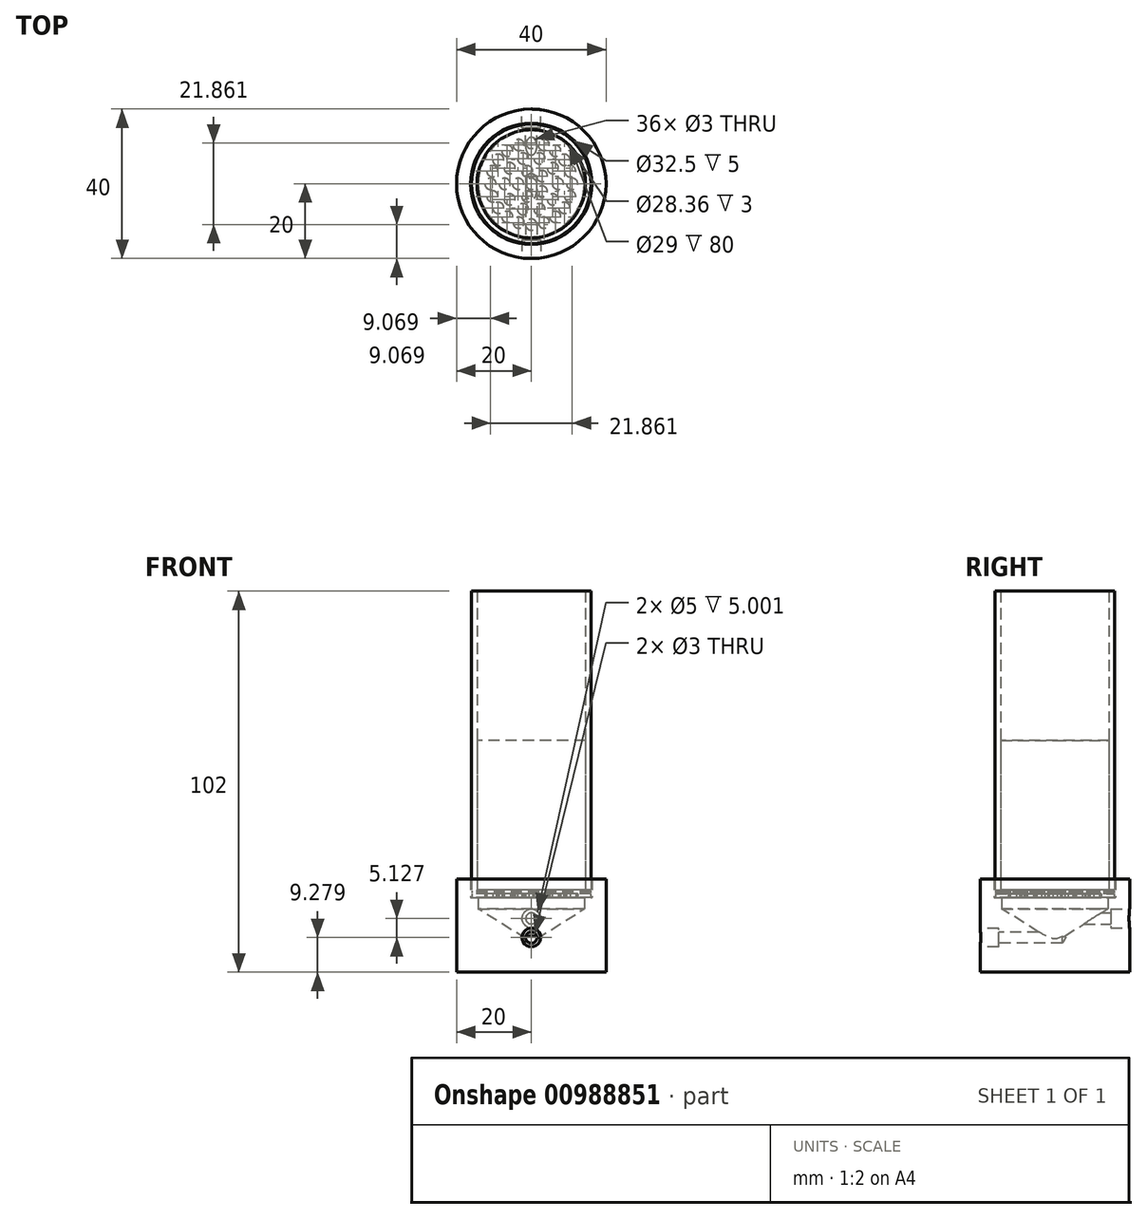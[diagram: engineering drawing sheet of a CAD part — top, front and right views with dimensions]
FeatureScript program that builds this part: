
annotation { "Feature Type Name" : "Feature", "Feature Type Description" : "" }
export const myFeature = defineFeature(function(context is Context, id is Id, definition is map)
    precondition{}
    {
        {
            var Q0;
            Q0=qCreatedBy(makeId("Top.planeOp"),FACE);
            var sketch = newSketch(context, id + "F0", { "sketchPlane" : qUnion([Q0])});
            skCircle(sketch, "E0", {"center": v(0, 0) * mm, "radius": 16 * mm});
            skCircle(sketch, "E1", {"center": v(0, 0) * mm, "radius": 14.5 * mm});
            skSolve(sketch);
        }
        {
            var Q0;
            Q0=makeQuery(id+"F0.imprint","IMPRINT",FACE,{"disambiguationData":[TD([[makeQuery(id+"F0.imprint","IMPRINT",EDGE,{"derivedFrom":sQuery(id+"F0.wireOp",EDGE,"E0")}),1.0]])]});
            extrude(context, id + "F1", {"entities" : qUnion([Q0]), "depth" : 80 * mm, "offsetDistance" : 25 * mm});
        }
        {
            var Q0;
            Q0=qCreatedBy(makeId("Front.planeOp"),FACE);
            var sketch = newSketch(context, id + "F2", { "sketchPlane" : qUnion([Q0])});
            skLineSegment(sketch, "E2", {"start": v(-16.25, 0) * mm, "end": v(-16.25, 5) * mm});
            skLineSegment(sketch, "E3", {"start": v(-16.25, 5) * mm, "end": v(-20, 5) * mm});
            skLineSegment(sketch, "E4", {"start": v(-20, 5) * mm, "end": v(-20, -20) * mm});
            skLineSegment(sketch, "E5", {"start": v(-20, -20) * mm, "end": v(0, -20) * mm});
            skLineSegment(sketch, "E6", {"start": v(0, -20) * mm, "end": v(0, -12) * mm});
            skLineSegment(sketch, "E7", {"start": v(0, -12) * mm, "end": v(-14.18, -3) * mm});
            skLineSegment(sketch, "E8", {"start": v(-14.18, -3) * mm, "end": v(-14.18, 0) * mm});
            skLineSegment(sketch, "E9", {"start": v(-14.18, 0) * mm, "end": v(-16.25, 0) * mm});
            skSolve(sketch);
        }
        {
            var Q0;
            Q0=makeQuery(id+"F2.imprint","IMPRINT",FACE,{"disambiguationData":[TD([[makeQuery(id+"F2.imprint","IMPRINT",EDGE,{"derivedFrom":sQuery(id+"F2.wireOp",EDGE,"E2")}),1.0]])]});
            var Q1;
            Q1=sQuery(id+"F2.wireOp",EDGE,"E6");
            revolve(context, id + "F3", {"surfaceOperationType" : NewSurfaceOperationType.NEW, "entities" : qUnion([Q0]), "axis" : qUnion([Q1]), "revolveType" : RevolveType.FULL});
        }
        {
            var Q0;
            Q0=qCreatedBy(makeId("Front.planeOp"),FACE);
            cPlane(context, id + "F4", {"entities" : qUnion([Q0]), "cplaneType" : CPlaneType.OFFSET, "offset" : 20 * mm, "width" : 150 * mm, "height" : 150 * mm});
        }
        {
            var Q0;
            Q0=qCreatedBy(id+"F4.planeOp",FACE);
            var sketch = newSketch(context, id + "F5", { "sketchPlane" : qUnion([Q0])});
            skLineSegment(sketch, "E10", {"start": v(0, -20.72) * mm, "end": v(0, -10.72) * mm});
            skSolve(sketch);
        }
        {
            var Q0;
            Q0=sQuery(id+"F5.wireOp",VERTEX,"E10.end");
            var Q1;
            Q1=makeQuery(id+"F3.opRevolve","SWEPT_BODY",BODY,{"disambiguationData":[OSD([sQuery(id+"F2.wireOp",EDGE,"E2"),sQuery(id+"F2.wireOp",EDGE,"E3"),sQuery(id+"F2.wireOp",EDGE,"E4"),sQuery(id+"F2.wireOp",EDGE,"E5"),sQuery(id+"F2.wireOp",EDGE,"E6"),sQuery(id+"F2.wireOp",EDGE,"E7"),sQuery(id+"F2.wireOp",EDGE,"E8"),sQuery(id+"F2.wireOp",EDGE,"E9")])]});
            hole(context, id + "F6", {"style" : HoleStyle.C_BORE, "endStyle" : HoleEndStyle.BLIND, "holeDiameter" : 3 * mm, "cBoreDiameter" : 5 * mm, "cBoreDepth" : 5 * mm, "majorDiameter" : 5 * mm, "holeDepth" : 22 * mm, "isTappedThrough" : true, "tappedDepth" : 12 * mm, "tapClearance" : 3, "startFromSketch" : true, "locations" : qUnion([Q0]), "scope" : qUnion([Q1])});
        }
        {
            var Q0;
            Q0=qCreatedBy(makeId("Front.planeOp"),FACE);
            cPlane(context, id + "F7", {"entities" : qUnion([Q0]), "cplaneType" : CPlaneType.OFFSET, "offset" : 20 * mm, "oppositeDirection" : true, "width" : 150 * mm, "height" : 150 * mm});
        }
        {
            var Q0;
            Q0=qCreatedBy(id+"F7.planeOp",FACE);
            var sketch = newSketch(context, id + "F8", { "sketchPlane" : qUnion([Q0])});
            skLineSegment(sketch, "E11", {"start": v(0, -19.77) * mm, "end": v(0, -5.6) * mm});
            skSolve(sketch);
        }
        {
            var Q0;
            Q0=sQuery(id+"F8.wireOp",VERTEX,"E11.end");
            var Q1;
            Q1=makeQuery(id+"F3.opRevolve","SWEPT_BODY",BODY,{"disambiguationData":[OSD([sQuery(id+"F2.wireOp",EDGE,"E2"),sQuery(id+"F2.wireOp",EDGE,"E3"),sQuery(id+"F2.wireOp",EDGE,"E4"),sQuery(id+"F2.wireOp",EDGE,"E5"),sQuery(id+"F2.wireOp",EDGE,"E6"),sQuery(id+"F2.wireOp",EDGE,"E7"),sQuery(id+"F2.wireOp",EDGE,"E8"),sQuery(id+"F2.wireOp",EDGE,"E9")])]});
            hole(context, id + "F9", {"style" : HoleStyle.C_BORE, "endStyle" : HoleEndStyle.BLIND, "oppositeDirection" : true, "holeDiameter" : 3 * mm, "cBoreDiameter" : 5 * mm, "cBoreDepth" : 5 * mm, "majorDiameter" : 5 * mm, "holeDepth" : 22 * mm, "isTappedThrough" : true, "tappedDepth" : 12 * mm, "tapClearance" : 3, "startFromSketch" : true, "locations" : qUnion([Q0]), "scope" : qUnion([Q1])});
        }
        {
            var Q0;
            Q0=makeQuery(id+"F1.opExtrude","SWEPT_BODY",BODY,{"disambiguationData":[OSD([sQuery(id+"F0.wireOp",EDGE,"E0"),sQuery(id+"F0.wireOp",EDGE,"E1")])]});
            transform(context, id + "F10", {"entities" : qUnion([Q0]), "transformType" : TransformType.TRANSLATION_3D, "dx" : 0 * mm, "dy" : 0 * mm, "dz" : 2 * mm, "makeCopy" : false});
        }
        {
            var Q0;
            Q0=qCreatedBy(makeId("Top.planeOp"),FACE);
            var sketch = newSketch(context, id + "F11", { "sketchPlane" : qUnion([Q0])});
            skCircle(sketch, "E12", {"center": v(0, 0) * mm, "radius": 15.9 * mm});
            skSolve(sketch);
        }
        {
            var Q0;
            Q0=makeQuery(id+"F11.imprint","IMPRINT",FACE,{"disambiguationData":[TD([[makeQuery(id+"F11.imprint","IMPRINT",EDGE,{"derivedFrom":sQuery(id+"F11.wireOp",EDGE,"E12")}),1.0]])]});
            extrude(context, id + "F12", {"entities" : qUnion([Q0]), "depth" : 1 * mm, "offsetDistance" : 25 * mm});
        }
        {
            var Q0;
            Q0=qCreatedBy(makeId("Top.planeOp"),FACE);
            var sketch = newSketch(context, id + "F13", { "sketchPlane" : qUnion([Q0])});
            skCircle(sketch, "E13", {"center": v(0, 0) * mm, "radius": 1.5 * mm});
            skCircle(sketch, "E14", {"center": v(-3.54, 0) * mm, "radius": 1.5 * mm});
            skCircle(sketch, "E15.1.0", {"center": v(-1.1, -3.36) * mm, "radius": 1.5 * mm});
            skCircle(sketch, "E15.2.0", {"center": v(2.86, -2.08) * mm, "radius": 1.5 * mm});
            skCircle(sketch, "E15.3.0", {"center": v(2.86, 2.08) * mm, "radius": 1.5 * mm});
            skCircle(sketch, "E15.4.0", {"center": v(-1.1, 3.36) * mm, "radius": 1.5 * mm});
            skCircle(sketch, "E16", {"center": v(-7.13, 0) * mm, "radius": 1.5 * mm});
            skCircle(sketch, "E17.1.0", {"center": v(-5.77, -4.19) * mm, "radius": 1.5 * mm});
            skCircle(sketch, "E17.2.0", {"center": v(-2.2, -6.78) * mm, "radius": 1.5 * mm});
            skCircle(sketch, "E17.3.0", {"center": v(2.2, -6.78) * mm, "radius": 1.5 * mm});
            skCircle(sketch, "E17.4.0", {"center": v(5.77, -4.19) * mm, "radius": 1.5 * mm});
            skCircle(sketch, "E17.5.0", {"center": v(7.13, 0) * mm, "radius": 1.5 * mm});
            skCircle(sketch, "E17.6.0", {"center": v(5.77, 4.19) * mm, "radius": 1.5 * mm});
            skCircle(sketch, "E17.7.0", {"center": v(2.2, 6.78) * mm, "radius": 1.5 * mm});
            skCircle(sketch, "E17.8.0", {"center": v(-2.2, 6.78) * mm, "radius": 1.5 * mm});
            skCircle(sketch, "E17.9.0", {"center": v(-5.77, 4.19) * mm, "radius": 1.5 * mm});
            skCircle(sketch, "E18", {"center": v(-10.93, 0) * mm, "radius": 1.5 * mm});
            skCircle(sketch, "E19.1.0", {"center": v(-10.4, -3.38) * mm, "radius": 1.5 * mm});
            skCircle(sketch, "E19.2.0", {"center": v(-8.84, -6.42) * mm, "radius": 1.5 * mm});
            skCircle(sketch, "E19.3.0", {"center": v(-6.42, -8.84) * mm, "radius": 1.5 * mm});
            skCircle(sketch, "E19.4.0", {"center": v(-3.38, -10.4) * mm, "radius": 1.5 * mm});
            skCircle(sketch, "E19.5.0", {"center": v(0, -10.93) * mm, "radius": 1.5 * mm});
            skCircle(sketch, "E19.6.0", {"center": v(3.38, -10.4) * mm, "radius": 1.5 * mm});
            skCircle(sketch, "E19.7.0", {"center": v(6.42, -8.84) * mm, "radius": 1.5 * mm});
            skCircle(sketch, "E19.8.0", {"center": v(8.84, -6.42) * mm, "radius": 1.5 * mm});
            skCircle(sketch, "E19.9.0", {"center": v(10.4, -3.38) * mm, "radius": 1.5 * mm});
            skCircle(sketch, "E19.10.0", {"center": v(10.93, 0) * mm, "radius": 1.5 * mm});
            skCircle(sketch, "E19.11.0", {"center": v(10.4, 3.38) * mm, "radius": 1.5 * mm});
            skCircle(sketch, "E19.12.0", {"center": v(8.84, 6.42) * mm, "radius": 1.5 * mm});
            skCircle(sketch, "E19.13.0", {"center": v(6.42, 8.84) * mm, "radius": 1.5 * mm});
            skCircle(sketch, "E19.14.0", {"center": v(3.38, 10.4) * mm, "radius": 1.5 * mm});
            skCircle(sketch, "E19.15.0", {"center": v(0, 10.93) * mm, "radius": 1.5 * mm});
            skCircle(sketch, "E19.16.0", {"center": v(-3.38, 10.4) * mm, "radius": 1.5 * mm});
            skCircle(sketch, "E19.17.0", {"center": v(-6.42, 8.84) * mm, "radius": 1.5 * mm});
            skCircle(sketch, "E19.18.0", {"center": v(-8.84, 6.42) * mm, "radius": 1.5 * mm});
            skCircle(sketch, "E19.19.0", {"center": v(-10.4, 3.38) * mm, "radius": 1.5 * mm});
            skSolve(sketch);
        }
        {
            var Q0;
            Q0=makeQuery(id+"F13.imprint","IMPRINT",FACE,{"disambiguationData":[TD([[makeQuery(id+"F13.imprint","IMPRINT",EDGE,{"derivedFrom":sQuery(id+"F13.wireOp",EDGE,"E19.7.0")}),1.0]])]});
            var Q1;
            Q1=makeQuery(id+"F13.imprint","IMPRINT",FACE,{"disambiguationData":[TD([[makeQuery(id+"F13.imprint","IMPRINT",EDGE,{"derivedFrom":sQuery(id+"F13.wireOp",EDGE,"E19.3.0")}),1.0]])]});
            var Q2;
            Q2=makeQuery(id+"F13.imprint","IMPRINT",FACE,{"disambiguationData":[TD([[makeQuery(id+"F13.imprint","IMPRINT",EDGE,{"derivedFrom":sQuery(id+"F13.wireOp",EDGE,"E19.1.0")}),1.0]])]});
            var Q3;
            Q3=makeQuery(id+"F13.imprint","IMPRINT",FACE,{"disambiguationData":[TD([[makeQuery(id+"F13.imprint","IMPRINT",EDGE,{"derivedFrom":sQuery(id+"F13.wireOp",EDGE,"E19.5.0")}),1.0]])]});
            var Q4;
            Q4=makeQuery(id+"F13.imprint","IMPRINT",FACE,{"disambiguationData":[TD([[makeQuery(id+"F13.imprint","IMPRINT",EDGE,{"derivedFrom":sQuery(id+"F13.wireOp",EDGE,"E19.17.0")}),1.0]])]});
            var Q5;
            Q5=makeQuery(id+"F13.imprint","IMPRINT",FACE,{"disambiguationData":[TD([[makeQuery(id+"F13.imprint","IMPRINT",EDGE,{"derivedFrom":sQuery(id+"F13.wireOp",EDGE,"E19.14.0")}),1.0]])]});
            var Q6;
            Q6=makeQuery(id+"F13.imprint","IMPRINT",FACE,{"disambiguationData":[TD([[makeQuery(id+"F13.imprint","IMPRINT",EDGE,{"derivedFrom":sQuery(id+"F13.wireOp",EDGE,"E19.19.0")}),1.0]])]});
            var Q7;
            Q7=makeQuery(id+"F13.imprint","IMPRINT",FACE,{"disambiguationData":[TD([[makeQuery(id+"F13.imprint","IMPRINT",EDGE,{"derivedFrom":sQuery(id+"F13.wireOp",EDGE,"E19.15.0")}),1.0]])]});
            var Q8;
            Q8=makeQuery(id+"F13.imprint","IMPRINT",FACE,{"disambiguationData":[TD([[makeQuery(id+"F13.imprint","IMPRINT",EDGE,{"derivedFrom":sQuery(id+"F13.wireOp",EDGE,"E17.9.0")}),1.0]])]});
            var Q9;
            Q9=makeQuery(id+"F13.imprint","IMPRINT",FACE,{"disambiguationData":[TD([[makeQuery(id+"F13.imprint","IMPRINT",EDGE,{"derivedFrom":sQuery(id+"F13.wireOp",EDGE,"E15.3.0")}),1.0]])]});
            var Q10;
            Q10=makeQuery(id+"F13.imprint","IMPRINT",FACE,{"disambiguationData":[TD([[makeQuery(id+"F13.imprint","IMPRINT",EDGE,{"derivedFrom":sQuery(id+"F13.wireOp",EDGE,"E17.1.0")}),1.0]])]});
            var Q11;
            Q11=makeQuery(id+"F13.imprint","IMPRINT",FACE,{"disambiguationData":[TD([[makeQuery(id+"F13.imprint","IMPRINT",EDGE,{"derivedFrom":sQuery(id+"F13.wireOp",EDGE,"E19.16.0")}),1.0]])]});
            var Q12;
            Q12=makeQuery(id+"F13.imprint","IMPRINT",FACE,{"disambiguationData":[TD([[makeQuery(id+"F13.imprint","IMPRINT",EDGE,{"derivedFrom":sQuery(id+"F13.wireOp",EDGE,"E19.8.0")}),1.0]])]});
            var Q13;
            Q13=makeQuery(id+"F13.imprint","IMPRINT",FACE,{"disambiguationData":[TD([[makeQuery(id+"F13.imprint","IMPRINT",EDGE,{"derivedFrom":sQuery(id+"F13.wireOp",EDGE,"E14")}),1.0]])]});
            var Q14;
            Q14=makeQuery(id+"F13.imprint","IMPRINT",FACE,{"disambiguationData":[TD([[makeQuery(id+"F13.imprint","IMPRINT",EDGE,{"derivedFrom":sQuery(id+"F13.wireOp",EDGE,"E17.2.0")}),1.0]])]});
            var Q15;
            Q15=makeQuery(id+"F13.imprint","IMPRINT",FACE,{"disambiguationData":[TD([[makeQuery(id+"F13.imprint","IMPRINT",EDGE,{"derivedFrom":sQuery(id+"F13.wireOp",EDGE,"E17.8.0")}),1.0]])]});
            var Q16;
            Q16=makeQuery(id+"F13.imprint","IMPRINT",FACE,{"disambiguationData":[TD([[makeQuery(id+"F13.imprint","IMPRINT",EDGE,{"derivedFrom":sQuery(id+"F13.wireOp",EDGE,"E19.12.0")}),1.0]])]});
            var Q17;
            Q17=makeQuery(id+"F13.imprint","IMPRINT",FACE,{"disambiguationData":[TD([[makeQuery(id+"F13.imprint","IMPRINT",EDGE,{"derivedFrom":sQuery(id+"F13.wireOp",EDGE,"E17.7.0")}),1.0]])]});
            var Q18;
            Q18=makeQuery(id+"F13.imprint","IMPRINT",FACE,{"disambiguationData":[TD([[makeQuery(id+"F13.imprint","IMPRINT",EDGE,{"derivedFrom":sQuery(id+"F13.wireOp",EDGE,"E19.13.0")}),1.0]])]});
            var Q19;
            Q19=makeQuery(id+"F13.imprint","IMPRINT",FACE,{"disambiguationData":[TD([[makeQuery(id+"F13.imprint","IMPRINT",EDGE,{"derivedFrom":sQuery(id+"F13.wireOp",EDGE,"E13")}),1.0]])]});
            var Q20;
            Q20=makeQuery(id+"F13.imprint","IMPRINT",FACE,{"disambiguationData":[TD([[makeQuery(id+"F13.imprint","IMPRINT",EDGE,{"derivedFrom":sQuery(id+"F13.wireOp",EDGE,"E19.9.0")}),1.0]])]});
            var Q21;
            Q21=makeQuery(id+"F13.imprint","IMPRINT",FACE,{"disambiguationData":[TD([[makeQuery(id+"F13.imprint","IMPRINT",EDGE,{"derivedFrom":sQuery(id+"F13.wireOp",EDGE,"E19.10.0")}),1.0]])]});
            var Q22;
            Q22=makeQuery(id+"F13.imprint","IMPRINT",FACE,{"disambiguationData":[TD([[makeQuery(id+"F13.imprint","IMPRINT",EDGE,{"derivedFrom":sQuery(id+"F13.wireOp",EDGE,"E17.6.0")}),1.0]])]});
            var Q23;
            Q23=makeQuery(id+"F13.imprint","IMPRINT",FACE,{"disambiguationData":[TD([[makeQuery(id+"F13.imprint","IMPRINT",EDGE,{"derivedFrom":sQuery(id+"F13.wireOp",EDGE,"E17.4.0")}),1.0]])]});
            var Q24;
            Q24=makeQuery(id+"F13.imprint","IMPRINT",FACE,{"disambiguationData":[TD([[makeQuery(id+"F13.imprint","IMPRINT",EDGE,{"derivedFrom":sQuery(id+"F13.wireOp",EDGE,"E19.11.0")}),1.0]])]});
            var Q25;
            Q25=makeQuery(id+"F13.imprint","IMPRINT",FACE,{"disambiguationData":[TD([[makeQuery(id+"F13.imprint","IMPRINT",EDGE,{"derivedFrom":sQuery(id+"F13.wireOp",EDGE,"E17.3.0")}),1.0]])]});
            var Q26;
            Q26=makeQuery(id+"F13.imprint","IMPRINT",FACE,{"disambiguationData":[TD([[makeQuery(id+"F13.imprint","IMPRINT",EDGE,{"derivedFrom":sQuery(id+"F13.wireOp",EDGE,"E16")}),1.0]])]});
            var Q27;
            Q27=makeQuery(id+"F13.imprint","IMPRINT",FACE,{"disambiguationData":[TD([[makeQuery(id+"F13.imprint","IMPRINT",EDGE,{"derivedFrom":sQuery(id+"F13.wireOp",EDGE,"E15.1.0")}),1.0]])]});
            var Q28;
            Q28=makeQuery(id+"F13.imprint","IMPRINT",FACE,{"disambiguationData":[TD([[makeQuery(id+"F13.imprint","IMPRINT",EDGE,{"derivedFrom":sQuery(id+"F13.wireOp",EDGE,"E19.6.0")}),1.0]])]});
            var Q29;
            Q29=makeQuery(id+"F13.imprint","IMPRINT",FACE,{"disambiguationData":[TD([[makeQuery(id+"F13.imprint","IMPRINT",EDGE,{"derivedFrom":sQuery(id+"F13.wireOp",EDGE,"E15.2.0")}),1.0]])]});
            var Q30;
            Q30=makeQuery(id+"F13.imprint","IMPRINT",FACE,{"disambiguationData":[TD([[makeQuery(id+"F13.imprint","IMPRINT",EDGE,{"derivedFrom":sQuery(id+"F13.wireOp",EDGE,"E15.4.0")}),1.0]])]});
            var Q31;
            Q31=makeQuery(id+"F13.imprint","IMPRINT",FACE,{"disambiguationData":[TD([[makeQuery(id+"F13.imprint","IMPRINT",EDGE,{"derivedFrom":sQuery(id+"F13.wireOp",EDGE,"E19.4.0")}),1.0]])]});
            var Q32;
            Q32=makeQuery(id+"F13.imprint","IMPRINT",FACE,{"disambiguationData":[TD([[makeQuery(id+"F13.imprint","IMPRINT",EDGE,{"derivedFrom":sQuery(id+"F13.wireOp",EDGE,"E19.2.0")}),1.0]])]});
            var Q33;
            Q33=makeQuery(id+"F13.imprint","IMPRINT",FACE,{"disambiguationData":[TD([[makeQuery(id+"F13.imprint","IMPRINT",EDGE,{"derivedFrom":sQuery(id+"F13.wireOp",EDGE,"E18")}),1.0]])]});
            var Q34;
            Q34=makeQuery(id+"F13.imprint","IMPRINT",FACE,{"disambiguationData":[TD([[makeQuery(id+"F13.imprint","IMPRINT",EDGE,{"derivedFrom":sQuery(id+"F13.wireOp",EDGE,"E19.18.0")}),1.0]])]});
            var Q35;
            Q35=makeQuery(id+"F13.imprint","IMPRINT",FACE,{"disambiguationData":[TD([[makeQuery(id+"F13.imprint","IMPRINT",EDGE,{"derivedFrom":sQuery(id+"F13.wireOp",EDGE,"E17.5.0")}),1.0]])]});
            extrude(context, id + "F14", {"entities" : qUnion([Q0, Q1, Q2, Q3, Q4, Q5, Q6, Q7, Q8, Q9, Q10, Q11, Q12, Q13, Q14, Q15, Q16, Q17, Q18, Q19, Q20, Q21, Q22, Q23, Q24, Q25, Q26, Q27, Q28, Q29, Q30, Q31, Q32, Q33, Q34, Q35]), "operationType" : NewBodyOperationType.REMOVE, "depth" : 1 * mm, "offsetDistance" : 25 * mm});
        }
        {
            var Q0;
            Q0=qCreatedBy(makeId("Top.planeOp"),FACE);
            var sketch = newSketch(context, id + "F15", { "sketchPlane" : qUnion([Q0])});
            skCircle(sketch, "E20", {"center": v(0, 0) * mm, "radius": 14.5 * mm});
            skSolve(sketch);
        }
        {
            var Q0;
            Q0=makeQuery(id+"F15.imprint","IMPRINT",FACE,{"disambiguationData":[TD([[makeQuery(id+"F15.imprint","IMPRINT",EDGE,{"derivedFrom":sQuery(id+"F15.wireOp",EDGE,"E20")}),1.0]])]});
            extrude(context, id + "F16", {"entities" : qUnion([Q0]), "depth" : 40 * mm, "offsetDistance" : 25 * mm});
        }
        {
            var Q0;
            Q0=makeQuery(id+"F16.opExtrude","SWEPT_BODY",BODY,{"disambiguationData":[OSD([sQuery(id+"F15.wireOp",EDGE,"E20")])]});
            transform(context, id + "F17", {"entities" : qUnion([Q0]), "transformType" : TransformType.TRANSLATION_3D, "dx" : 0 * mm, "dy" : 0 * mm, "dz" : 2 * mm, "makeCopy" : false});
        }
        {
            var Q0;
            Q0=qCreatedBy(makeId("Top.planeOp"),FACE);
            var sketch = newSketch(context, id + "F18", { "sketchPlane" : qUnion([Q0])});
            skCircle(sketch, "E21", {"center": v(0, 0) * mm, "radius": 15.9 * mm});
            skSolve(sketch);
        }
        {
            var Q0;
            Q0=makeQuery(id+"F18.imprint","IMPRINT",FACE,{"disambiguationData":[TD([[makeQuery(id+"F18.imprint","IMPRINT",EDGE,{"derivedFrom":sQuery(id+"F18.wireOp",EDGE,"E21")}),1.0]])]});
            extrude(context, id + "F19", {"entities" : qUnion([Q0]), "depth" : 0.5 * mm, "offsetDistance" : 25 * mm});
        }
        {
            var Q0;
            Q0=makeQuery(id+"F19.opExtrude","SWEPT_BODY",BODY,{"disambiguationData":[OSD([sQuery(id+"F18.wireOp",EDGE,"E21")])]});
            transform(context, id + "F20", {"entities" : qUnion([Q0]), "transformType" : TransformType.TRANSLATION_3D, "dx" : 0 * mm, "dy" : 0 * mm, "dz" : 1.25 * mm, "makeCopy" : false});
        }
    });
